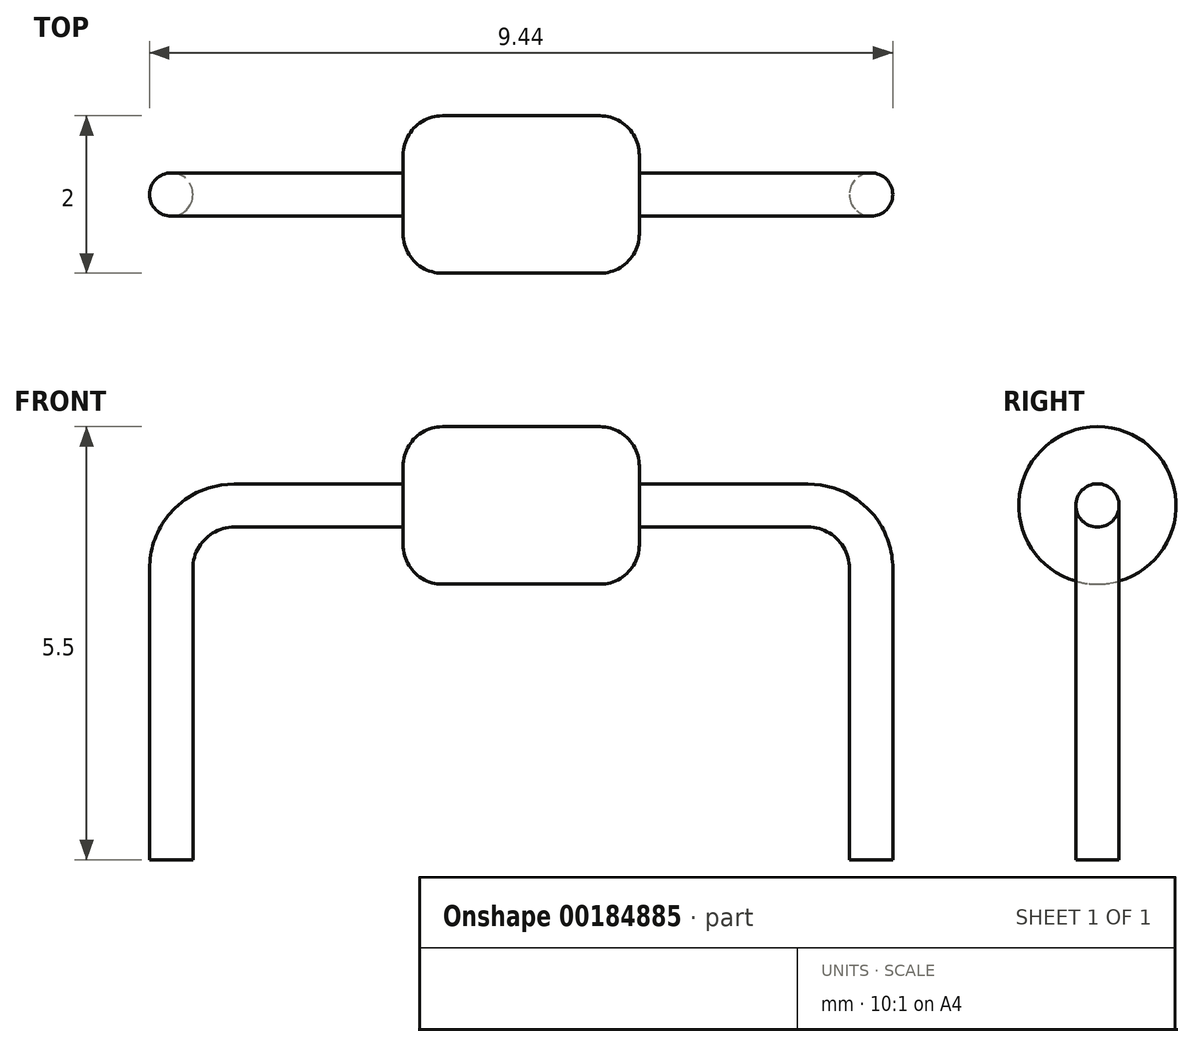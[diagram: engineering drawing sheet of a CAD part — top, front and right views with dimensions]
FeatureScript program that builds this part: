
annotation { "Feature Type Name" : "Feature", "Feature Type Description" : "" }
export const myFeature = defineFeature(function(context is Context, id is Id, definition is map)
    precondition{}
    {
        {
            var Q0;
            Q0=qCreatedBy(makeId("Top.planeOp"),FACE);
            var sketch = newSketch(context, id + "F0", { "sketchPlane" : qUnion([Q0])});
            skLineSegment(sketch, "E0", {"start": v(0, 1) * mm, "end": v(0, 0) * mm});
            skLineSegment(sketch, "E1", {"start": v(0, 0) * mm, "end": v(-1.5, 0) * mm});
            skLineSegment(sketch, "E2", {"start": v(-1, 1) * mm, "end": v(0, 1) * mm});
            skLineSegment(sketch, "E3", {"start": v(-1.5, 0.5) * mm, "end": v(-1.5, 0) * mm});
            skPoint(sketch, "E4.visualSharp", {"position": v(-1.5, 1) * mm});
            skArc(sketch, "E4.filletArc", {"start": v(-1, 1) * mm, "mid": v(-1.35, 0.85) * mm, "end": v(-1.5, 0.5) * mm});
            skSolve(sketch);
        }
        {
            var Q0;
            Q0=qSketchRegion(id+"F0",true);
            var Q1;
            Q1=sQuery(id+"F0.wireOp",EDGE,"E1");
            revolve(context, id + "F1", {"entities" : qUnion([Q0]), "axis" : qUnion([Q1]), "revolveType" : RevolveType.FULL});
        }
        {
            var Q0;
            Q0=makeQuery(id+"F1.opRevolve","SWEPT_BODY",BODY,{"disambiguationData":[OSD([sQuery(id+"F0.wireOp",EDGE,"R6nNJyvy-jtOy-Oz0t-GdW3-rGYJLNjDhLs3"),sQuery(id+"F0.wireOp",EDGE,"OYrOV2Nd-kG9M-vQlE-hcPz-iycsfkF3bxij"),sQuery(id+"F0.wireOp",EDGE,"CKmc3pMQ-ZjUI-Nwz4-CXNq-rJvErFQjkOrT"),sQuery(id+"F0.wireOp",EDGE,"mZ0JTMax-BH6E-OSVq-CJxj-MZuzuwoxwJZM"),sQuery(id+"F0.wireOp",EDGE,"E0"),sQuery(id+"F0.wireOp",EDGE,"E1"),sQuery(id+"F0.wireOp",EDGE,"f8288d26-9c1f-4e7e-8f55-05d16ea3eb06.filletArc"),sQuery(id+"F0.wireOp",EDGE,"eae6405c-0333-4a9e-afa1-58c621c1c707.filletArc"),sQuery(id+"F0.wireOp",EDGE,"36c53506-6451-4d1c-b3d5-b8041e847a99.filletArc")])]});
            var Q1;
            Q1=makeQuery(id+"F1.opRevolve","SWEPT_FACE",FACE,{"disambiguationData":[OSD([sQuery(id+"F0.wireOp",EDGE,"E0")])]});
            mirror(context, id + "F2", {"operationType" : NewBodyOperationType.ADD, "entities" : qUnion([Q0]), "mirrorPlane" : qUnion([Q1])});
        }
        {
            var Q0;
            Q0=qCreatedBy(makeId("Right.planeOp"),FACE);
            var sketch = newSketch(context, id + "F3", { "sketchPlane" : qUnion([Q0])});
            skCircle(sketch, "E5", {"center": v(0, 0) * mm, "radius": 0.28 * mm});
            skSolve(sketch);
        }
        {
            var Q0;
            Q0=qCreatedBy(makeId("Front.planeOp"),FACE);
            var sketch = newSketch(context, id + "F4", { "sketchPlane" : qUnion([Q0])});
            skLineSegment(sketch, "E6", {"start": v(0, 0) * mm, "end": v(3.65, 0) * mm});
            skLineSegment(sketch, "E7", {"start": v(4.45, -0.8) * mm, "end": v(4.45, -4.5) * mm});
            skPoint(sketch, "E8.visualSharp", {"position": v(4.44, 0) * mm});
            skArc(sketch, "E8.filletArc", {"start": v(4.45, -0.8) * mm, "mid": v(4.21, -0.23) * mm, "end": v(3.65, 0) * mm});
            skSolve(sketch);
        }
        {
            var Q0;
            Q0=qSketchRegion(id+"F3",true);
            var Q1;
            Q1=qConstructionFilter(qBodyType(qCreatedBy(id+"F4",EDGE),BodyType.WIRE),ConstructionObject.NO);
            sweep(context, id + "F5", {"profiles" : qUnion([Q0]), "path" : qUnion([Q1])});
        }
        {
            var Q0;
            Q0=makeQuery(id+"F5.opSweep","SWEPT_BODY",BODY,{"disambiguationData":[OSD([sQuery(id+"F3.wireOp",EDGE,"E5"),sQuery(id+"F4.wireOp",EDGE,"E6")])]});
            var Q1;
            Q1=qCreatedBy(makeId("Right.planeOp"),FACE);
            mirror(context, id + "F6", {"operationType" : NewBodyOperationType.ADD, "entities" : qUnion([Q0]), "mirrorPlane" : qUnion([Q1])});
        }
    });
